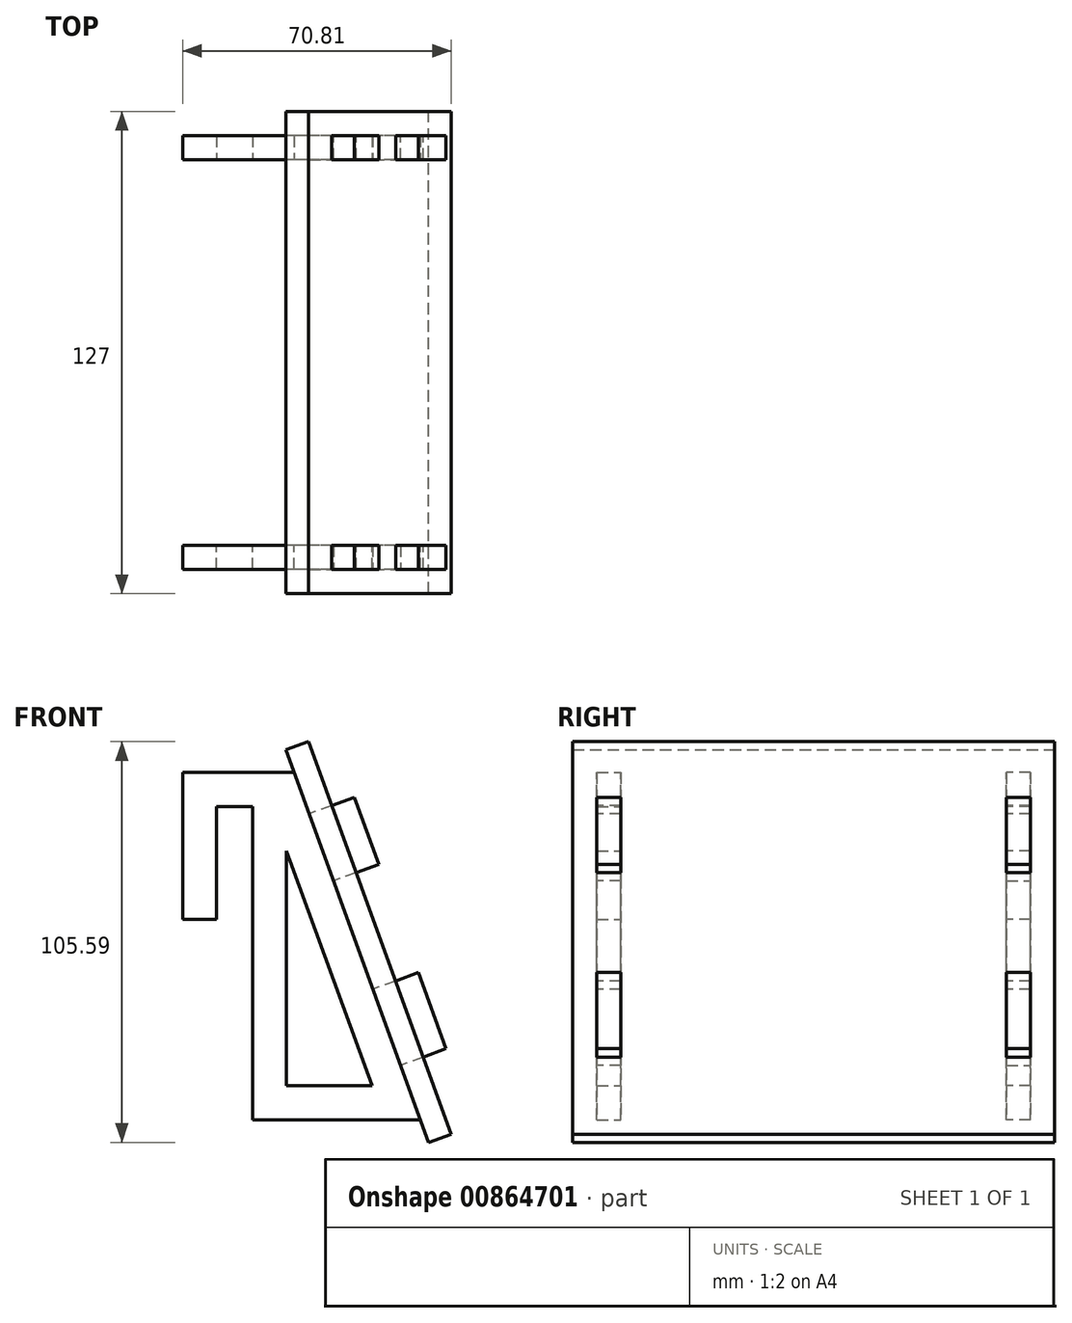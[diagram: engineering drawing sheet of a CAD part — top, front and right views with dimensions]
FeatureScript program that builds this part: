
annotation { "Feature Type Name" : "Feature", "Feature Type Description" : "" }
export const myFeature = defineFeature(function(context is Context, id is Id, definition is map)
    precondition{}
    {
        {
            assignVariable(context, id + "F0", {"name" : "thickness", "anyValue" : 6.35});
        }
        {
            var Q0;
            Q0=qCreatedBy(makeId("Front.planeOp"),FACE);
            cPlane(context, id + "F1", {"entities" : qUnion([Q0]), "cplaneType" : CPlaneType.OFFSET, "offset" : 50.8 * mm, "width" : 150 * mm, "height" : 150 * mm});
        }
        {
            var Q0;
            Q0=qCreatedBy(id+"F1.planeOp",FACE);
            var sketch = newSketch(context, id + "F2", { "sketchPlane" : qUnion([Q0])});
            skLineSegment(sketch, "E0", {"start": v(8.94, 0) * mm, "end": v(8.94, 29.82) * mm});
            skLineSegment(sketch, "E1", {"start": v(8.94, 29.82) * mm, "end": v(18.46, 29.82) * mm});
            skLineSegment(sketch, "E2", {"start": v(18.46, 29.82) * mm, "end": v(18.46, -52.73) * mm});
            skLineSegment(sketch, "E3", {"start": v(18.46, -52.73) * mm, "end": v(62.67, -52.73) * mm});
            skLineSegment(sketch, "E4", {"start": v(62.67, -52.73) * mm, "end": v(29.37, 38.75) * mm});
            skLineSegment(sketch, "E5", {"start": v(29.37, 38.75) * mm, "end": v(0, 38.75) * mm});
            skLineSegment(sketch, "E6", {"start": v(0, 38.75) * mm, "end": v(0, 0) * mm});
            skLineSegment(sketch, "E7", {"start": v(0, 0) * mm, "end": v(8.94, 0) * mm});
            skLineSegment(sketch, "E8", {"start": v(13.7, 29.82) * mm, "end": v(13.7, 38.75) * mm, "construction": true});
            skLineSegment(sketch, "E9.0", {"start": v(49.9, -43.8) * mm, "end": v(27.4, 18.04) * mm});
            skLineSegment(sketch, "E9.1", {"start": v(27.4, -43.8) * mm, "end": v(49.9, -43.8) * mm});
            skLineSegment(sketch, "E9.2", {"start": v(27.4, 18.04) * mm, "end": v(27.4, -43.8) * mm});
            skLineSegment(sketch, "E10", {"start": v(38.65, -43.8) * mm, "end": v(38.65, -52.73) * mm, "construction": true});
            skSolve(sketch);
        }
        {
            var Q0;
            Q0=makeQuery(id+"F2.imprint","IMPRINT",FACE,{"disambiguationData":[TD([[makeQuery(id+"F2.imprint","IMPRINT",EDGE,{"derivedFrom":sQuery(id+"F2.wireOp",EDGE,"E0")}),1.0]])]});
            extrude(context, id + "F3", {"entities" : qUnion([Q0]), "depth" : (getVariable(context, 'thickness')) * mm, "offsetDistance" : 25 * mm});
        }
        {
            var Q0;
            Q0=makeQuery(id+"F3.opExtrude","SWEPT_FACE",FACE,{"disambiguationData":[OSD([sQuery(id+"F2.wireOp",EDGE,"E4")])]});
            var sketch = newSketch(context, id + "F4", { "sketchPlane" : qUnion([Q0])});
            skLineSegment(sketch, "E11.0.0", {"start": v(-50.8, -70.99) * mm, "end": v(-50.8, 26.37) * mm});
            skLineSegment(sketch, "E11.0.1", {"start": v(-50.8, 26.37) * mm, "end": v(-57.15, 26.37) * mm});
            skLineSegment(sketch, "E11.0.2", {"start": v(-57.15, 26.37) * mm, "end": v(-57.15, -70.99) * mm});
            skLineSegment(sketch, "E11.0.3", {"start": v(-57.15, -70.99) * mm, "end": v(-50.8, -70.99) * mm});
            skLineSegment(sketch, "E12.bottom", {"start": v(-50.8, 14.77) * mm, "end": v(-57.15, 14.77) * mm});
            skLineSegment(sketch, "E12.top", {"start": v(-50.8, -3.98) * mm, "end": v(-57.15, -3.98) * mm});
            skLineSegment(sketch, "E12.left", {"start": v(-50.8, 14.77) * mm, "end": v(-50.8, -3.98) * mm});
            skLineSegment(sketch, "E12.right", {"start": v(-57.15, 14.77) * mm, "end": v(-57.15, -3.98) * mm});
            skLineSegment(sketch, "E13.bottom", {"start": v(-50.8, -34.37) * mm, "end": v(-57.15, -34.37) * mm});
            skLineSegment(sketch, "E13.top", {"start": v(-50.8, -55.72) * mm, "end": v(-57.15, -55.72) * mm});
            skLineSegment(sketch, "E13.left", {"start": v(-50.8, -34.37) * mm, "end": v(-50.8, -55.72) * mm});
            skLineSegment(sketch, "E13.right", {"start": v(-57.15, -34.37) * mm, "end": v(-57.15, -55.72) * mm});
            skSolve(sketch);
        }
        {
            var Q0;
            Q0=makeQuery(id+"F4.imprint","IMPRINT",FACE,{"disambiguationData":[TD([[makeQuery(id+"F4.imprint","IMPRINT",EDGE,{"derivedFrom":sQuery(id+"F4.wireOp",EDGE,"E12.bottom")}),1.0]])]});
            var Q1;
            Q1=makeQuery(id+"F4.imprint","IMPRINT",FACE,{"disambiguationData":[TD([[makeQuery(id+"F4.imprint","IMPRINT",EDGE,{"derivedFrom":sQuery(id+"F4.wireOp",EDGE,"E13.bottom")}),1.0]])]});
            extrude(context, id + "F5", {"entities" : qUnion([Q0, Q1]), "operationType" : NewBodyOperationType.ADD, "depth" : (2 * getVariable(context, 'thickness')) * mm, "offsetDistance" : 25 * mm});
        }
        {
            var Q0;
            Q0=makeQuery(id+"F3.opExtrude","SWEPT_BODY",BODY,{"disambiguationData":[OSD([sQuery(id+"F2.wireOp",EDGE,"E0"),sQuery(id+"F2.wireOp",EDGE,"E1"),sQuery(id+"F2.wireOp",EDGE,"E2"),sQuery(id+"F2.wireOp",EDGE,"E3"),sQuery(id+"F2.wireOp",EDGE,"E4"),sQuery(id+"F2.wireOp",EDGE,"E5"),sQuery(id+"F2.wireOp",EDGE,"E6"),sQuery(id+"F2.wireOp",EDGE,"E7"),sQuery(id+"F2.wireOp",EDGE,"E9.0"),sQuery(id+"F2.wireOp",EDGE,"E9.1"),sQuery(id+"F2.wireOp",EDGE,"E9.2")])]});
            var Q1;
            Q1=qCreatedBy(makeId("Front.planeOp"),FACE);
            mirror(context, id + "F6", {"entities" : qUnion([Q0]), "mirrorPlane" : qUnion([Q1])});
        }
        {
            var Q0;
            {var subQ5=sQuery(id+"F2.wireOp",EDGE,"E5");var subQ6=sQuery(id+"F2.wireOp",EDGE,"E4");Q0=makeQuery(id+"F5.boolean.opBoolean","SPLIT",FACE,{"disambiguationData":[TD([makeQuery(id+"F3.opExtrude","SWEPT_FACE",FACE,{"disambiguationData":[OSD([subQ5])]})])],"derivedFrom":makeQuery(id+"F3.opExtrude","SWEPT_FACE",FACE,{"disambiguationData":[OSD([subQ6])]})});}
            var sketch = newSketch(context, id + "F7", { "sketchPlane" : qUnion([Q0])});
            skLineSegment(sketch, "E14.bottom", {"start": v(-63.5, 32.72) * mm, "end": v(63.5, 32.72) * mm});
            skLineSegment(sketch, "E14.top", {"start": v(-63.5, -77.34) * mm, "end": v(63.5, -77.34) * mm});
            skLineSegment(sketch, "E14.left", {"start": v(-63.5, 32.72) * mm, "end": v(-63.5, -77.34) * mm});
            skLineSegment(sketch, "E14.right", {"start": v(63.5, 32.72) * mm, "end": v(63.5, -77.34) * mm});
            skPoint(sketch, "E15.0", {"position": v(-57.15, 20.57) * mm});
            skLineSegment(sketch, "E16.0.0", {"start": v(-57.15, 14.77) * mm, "end": v(-50.8, 14.77) * mm, "construction": true});
            skLineSegment(sketch, "E16.0.1", {"start": v(-50.8, 14.77) * mm, "end": v(-50.8, 26.37) * mm, "construction": true});
            skLineSegment(sketch, "E16.0.2", {"start": v(-50.8, 26.37) * mm, "end": v(-57.15, 26.37) * mm, "construction": true});
            skLineSegment(sketch, "E16.0.3", {"start": v(-57.15, 26.37) * mm, "end": v(-57.15, 14.77) * mm, "construction": true});
            skLineSegment(sketch, "E17.0.0", {"start": v(50.8, -55.72) * mm, "end": v(50.8, -70.99) * mm, "construction": true});
            skLineSegment(sketch, "E17.0.1", {"start": v(50.8, -70.99) * mm, "end": v(57.15, -70.99) * mm, "construction": true});
            skLineSegment(sketch, "E17.0.2", {"start": v(57.15, -70.99) * mm, "end": v(57.15, -55.72) * mm, "construction": true});
            skLineSegment(sketch, "E17.0.3", {"start": v(57.15, -55.72) * mm, "end": v(50.8, -55.72) * mm, "construction": true});
            skLineSegment(sketch, "E18", {"start": v(-57.15, 26.37) * mm, "end": v(-63.5, 26.37) * mm, "construction": true});
            skLineSegment(sketch, "E19", {"start": v(-63.5, 26.37) * mm, "end": v(-57.15, 26.37) * mm, "construction": true});
            skLineSegment(sketch, "E20", {"start": v(-57.15, 32.72) * mm, "end": v(-57.15, 26.37) * mm, "construction": true});
            skLineSegment(sketch, "E21", {"start": v(57.15, -70.99) * mm, "end": v(57.15, -77.34) * mm, "construction": true});
            skLineSegment(sketch, "E22", {"start": v(57.15, -77.34) * mm, "end": v(57.15, -70.99) * mm, "construction": true});
            skLineSegment(sketch, "E23", {"start": v(63.5, -70.99) * mm, "end": v(57.15, -70.99) * mm, "construction": true});
            skLineSegment(sketch, "E24.0.0", {"start": v(-57.15, -3.98) * mm, "end": v(-50.8, -3.98) * mm});
            skLineSegment(sketch, "E24.0.1", {"start": v(-50.8, -3.98) * mm, "end": v(-50.8, 14.77) * mm});
            skLineSegment(sketch, "E24.0.2", {"start": v(-50.8, 14.77) * mm, "end": v(-57.15, 14.77) * mm});
            skLineSegment(sketch, "E24.0.3", {"start": v(-57.15, 14.77) * mm, "end": v(-57.15, -3.98) * mm});
            skLineSegment(sketch, "E25.0.0", {"start": v(-57.15, -55.72) * mm, "end": v(-50.8, -55.72) * mm});
            skLineSegment(sketch, "E25.0.1", {"start": v(-50.8, -55.72) * mm, "end": v(-50.8, -34.37) * mm});
            skLineSegment(sketch, "E25.0.2", {"start": v(-50.8, -34.37) * mm, "end": v(-57.15, -34.37) * mm});
            skLineSegment(sketch, "E25.0.3", {"start": v(-57.15, -34.37) * mm, "end": v(-57.15, -55.72) * mm});
            skLineSegment(sketch, "E26.0.0", {"start": v(50.8, -3.98) * mm, "end": v(57.15, -3.98) * mm});
            skLineSegment(sketch, "E26.0.1", {"start": v(57.15, -3.98) * mm, "end": v(57.15, 14.77) * mm});
            skLineSegment(sketch, "E26.0.2", {"start": v(57.15, 14.77) * mm, "end": v(50.8, 14.77) * mm});
            skLineSegment(sketch, "E26.0.3", {"start": v(50.8, 14.77) * mm, "end": v(50.8, -3.98) * mm});
            skLineSegment(sketch, "E27.0.0", {"start": v(50.8, -55.72) * mm, "end": v(57.15, -55.72) * mm});
            skLineSegment(sketch, "E27.0.1", {"start": v(57.15, -55.72) * mm, "end": v(57.15, -34.37) * mm});
            skLineSegment(sketch, "E27.0.2", {"start": v(57.15, -34.37) * mm, "end": v(50.8, -34.37) * mm});
            skLineSegment(sketch, "E27.0.3", {"start": v(50.8, -34.37) * mm, "end": v(50.8, -55.72) * mm});
            skSolve(sketch);
        }
        {
            var Q0;
            Q0 = qSketchRegion(id + "F7", true);
            extrude(context, id + "F8", {"entities" : qUnion([Q0]), "depth" : (getVariable(context, 'thickness')) * mm, "offsetDistance" : 25 * mm});
        }
    });
